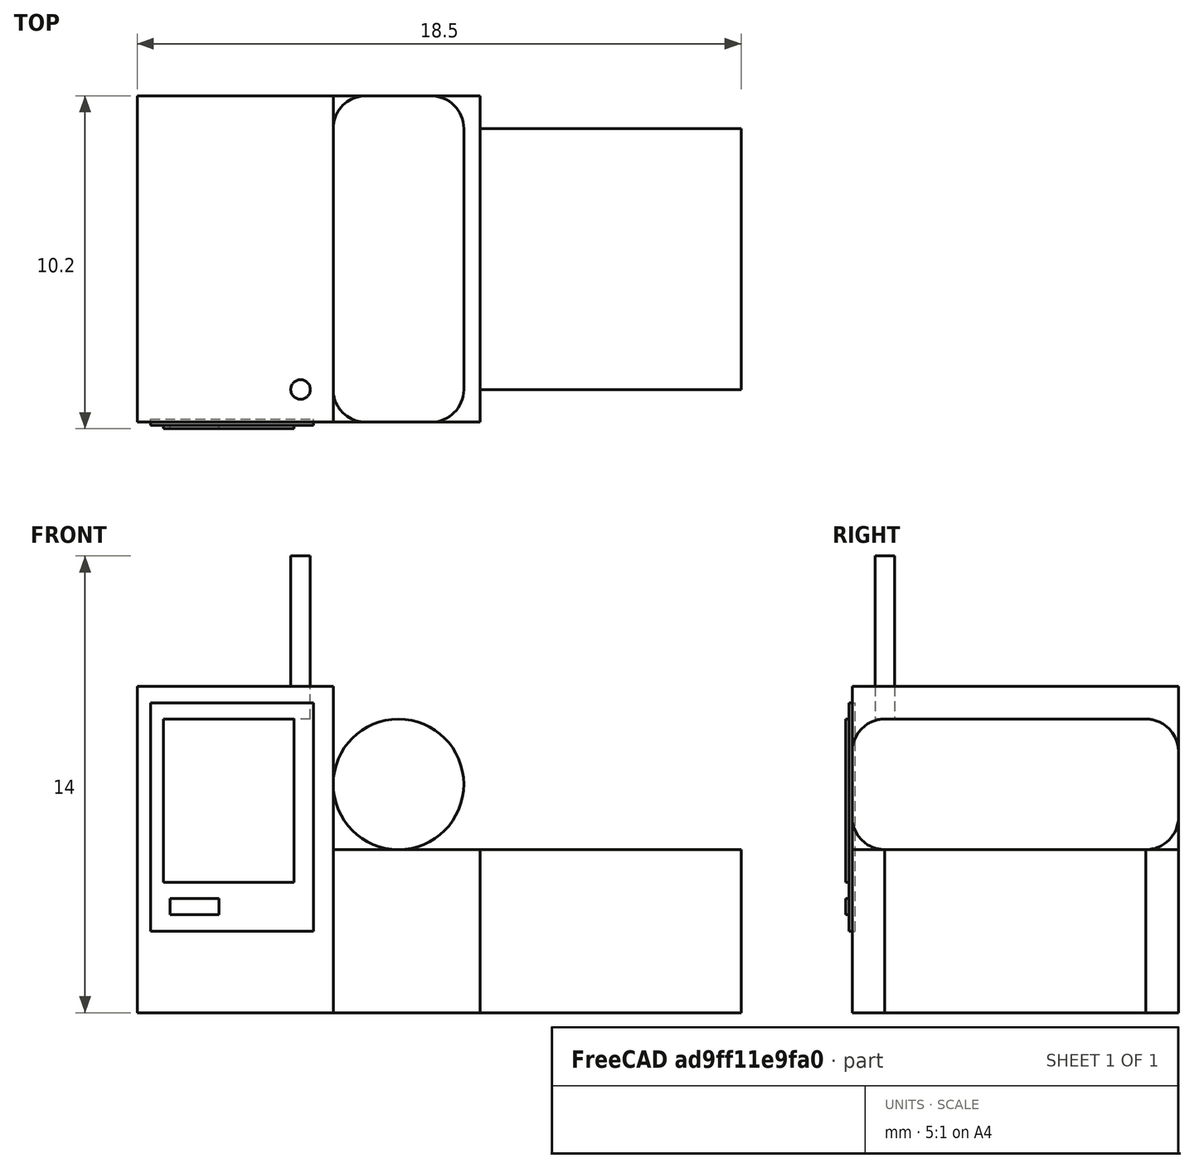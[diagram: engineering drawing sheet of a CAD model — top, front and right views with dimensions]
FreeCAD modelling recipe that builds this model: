
FCSTD DOCUMENT  (FreeCAD 0.20R29603 (Git))
Label: camio
License: All rights reserved
LicenseURL: http://en.wikipedia.org/wiki/All_rights_reserved
objects: Part::Box×6, Part::Cylinder×2, Part::Fillet×1
note: 9 computed .brp shape members not serialized (recipe doc carries the construction recipe); baked Part::Feature solids carry a one-line shape summary decoded from their .brp

FEATURE [Part::Box] Box  label="Cap Camio"
  AttacherType = Attacher::AttachEngine3D
  Height = 10
  Length = 6
  Width = 10
FEATURE [Part::Box] Box001  label="Darrer camio"
  AttacherType = Attacher::AttachEngine3D
  Height = 5
  Length = 4.5
  Placement = pos=(6,0,0) rot=(0,0,1;0rad)
  Width = 10
FEATURE [Part::Cylinder] Cylinder  label="Cilindre"
  Angle = 360
  AttacherType = Attacher::AttachEngine3D
  FirstAngle = 0
  Height = 10
  Placement = pos=(8,10,7) rot=(1,0,0;1.5708rad)
  Radius = 2
  SecondAngle = 0
FEATURE [Part::Fillet] Fillet  label="Combustible"
  Base = -> Cylinder
  Edges = 2 edges r=1: [Edge2,Edge3]
FEATURE [Part::Box] Box002  label="Finestra"
  AttacherType = Attacher::AttachEngine3D
  Height = 5
  Length = 4
  Placement = pos=(0.8,-0.2,4) rot=(0,0,1;0rad)
  Width = 0.1
FEATURE [Part::Box] Box003  label="Porta"
  AttacherType = Attacher::AttachEngine3D
  Height = 7
  Length = 5
  Placement = pos=(0.4,-0.1,2.5) rot=(0,0,1;0rad)
  Width = 0.2
FEATURE [Part::Box] Box004  label="Maneta"
  AttacherType = Attacher::AttachEngine3D
  Height = 0.5
  Length = 1.5
  Placement = pos=(1,-0.2,3) rot=(0,0,1;0rad)
  Width = 0.1
FEATURE [Part::Cylinder] Cylinder001  label="Cilindre001"
  Angle = 360
  AttacherType = Attacher::AttachEngine3D
  FirstAngle = 0
  Height = 5
  Placement = pos=(5,1,9) rot=(0,0,1;0rad)
  Radius = 0.3
  SecondAngle = 0
FEATURE [Part::Box] Box005  label="Cub"
  AttacherType = Attacher::AttachEngine3D
  Height = 5
  Length = 8
  Placement = pos=(10.5,1,0) rot=(0,0,1;0rad)
  Width = 8
